# Revit family: 873-00-002-DN300-400
name_source: partatom
category: Pipe Accessories
units: mm (PartAtom-declared; Revit-internal decimal feet)

## family parameters
Always vertical = Yes
Cut with Voids When Loaded = No
Part Type = Valve - Breaks Into
Round Connector Dimension = Use Diameter
Shared = No
Work Plane-Based = No

## types (3) — shared parameters
873-0300-00-741000 = DN300_PN25
873-0350-00-741000 = DN350_PN25
873-0400-00-741000 = DN400_PN25
Angle = 22.50°
Body_Wallthicknss = 10 mm  [stored 0.0328084 ft]
Description_ = AVK DISMANTLING JOINT
Flange_thickness = 20 mm  [stored 0.0656168 ft]
Search_table = 873-00-002-DN300-400
URL product pages = https://www.avkvalves.com

## per-type parameters (varying)
| type | A | DN | Id(Radius) | L | T | d1 | d2 |
| DN300 | 225 mm  [stored 0.738189 ft] | 300 mm  [stored 0.984252 ft] | 150 mm | 460 mm  [stored 1.50919 ft] | 27 mm  [stored 0.0885827 ft] | 430 mm | 243 mm |
| DN350 | 245 mm  [stored 0.803806 ft] | 350 mm  [stored 1.14829 ft] | 175 mm  [stored 0.574147 ft] | 480 mm  [stored 1.5748 ft] | 30 mm  [stored 0.0984252 ft] | 490 mm  [stored 1.60761 ft] | 278 mm |
| DN400 | 255 mm  [stored 0.836614 ft] | 400 mm  [stored 1.31234 ft] | 200 mm  [stored 0.656168 ft] | 500 mm  [stored 1.64042 ft] | 33 mm  [stored 0.108268 ft] | 550 mm  [stored 1.80446 ft] | 310 mm  [stored 1.01706 ft] |

note: [stored X ft] marks values corroborated as IEEE doubles in the binary element streams (Revit-internal decimal feet)

## geometry (parser evidence)
native form markers: Sweep x9
no freeform markers — native parametric forms only
